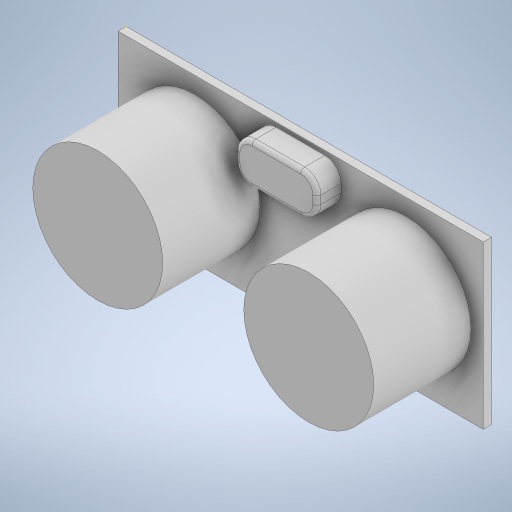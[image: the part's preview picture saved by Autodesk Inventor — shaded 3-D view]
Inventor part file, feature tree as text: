
AUTODESK INVENTOR PART (.ipt)
format: ipt  version: 2024.2 (Build 282272000, 272)  size: 286,720 bytes
history: native  units: mm
features: sketch x4, extrude x3, fillet x2
ambient origin geometry x8: Origin, YZ Plane, XZ Plane, XY Plane, X Axis, Y Axis, Z Axis, Center Point
bodies: Solid1 (feature_tree)
feature tree (9):
  extrude  "Extrusion1"  Depth=20.0mm
  extrude  "Extrusion2"  Depth=1.0mm
  extrude  "Extrusion3"  Depth=10.0mm
  fillet  "Fillet1"  Radius=10.0mm
  fillet  "Fillet2"  Radius=9.5mm
  sketch  "Sketch4"  dims[d9=12.0mm d10=0.0mm d11=10.0mm d12=5.0mm d13=17.5mm d14=0.5mm d15=3.0mm d16=0.0mm d17=2.0mm d18=0.5mm]
  sketch  "Sketch1"  dims[d0=45.0mm d1=20.0mm]
  sketch  "Sketch2"  dims[d2=1.0mm d3=0.0mm d4=16.0mm]
  sketch  "Sketch3"  dims[d5=16.0mm d6=26.0mm d7=10.0mm d8=9.5mm]
